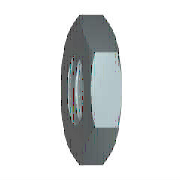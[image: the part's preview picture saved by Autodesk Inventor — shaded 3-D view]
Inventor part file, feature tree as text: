
AUTODESK INVENTOR PART (.ipt)
format: ipt  version: 2015 (Build 190159000, 159)  size: 172,544 bytes
history: native  units: mm (DEFAULTED — no unit token found)
features: sketch x3, chamfer x1, hole x1, other x1, plane x1
ambient origin geometry x7: Origin, YZ Plane, XZ Plane, X Axis, Y Axis, Z Axis, Center Point
bodies: Solid1 (feature_tree), Body (feature_tree)
feature tree (7):
  chamfer  "Chamfer1"  Angle=30.0deg  [1 undecoded]
  hole  "Thread"  [1 undecoded]
  other  "Work Axis1"
  plane  "Work Plane1"
  sketch  "Sketch1"  dims[d0=10.998523mm]
  sketch  "Sketch2"  dims[d1=3.302mm]
  sketch  "Sketch3"  dims[d2=0.0mm d3=30.0deg d4=30.0deg d5=9.525mm d6=9.525mm d7=90.0deg d25=3.683mm d26=6.0mm d27=4.0mm d28=2.0mm d29=14.3117mm d30=8.0mm d31=20.594885mm d8=0.57284mm d9=30.0deg d10=0.57284mm d11=30.0deg d13=0.0mm d14=0.0mm d39=0.0mm d40=0.57284mm d41=0.57284mm d42=0.0mm]
note: 2 required parameter values undecoded (feature->parameter linkage not recoverable at this tier; creation-order binding heuristic only, values carry confidence <= 0.55)
